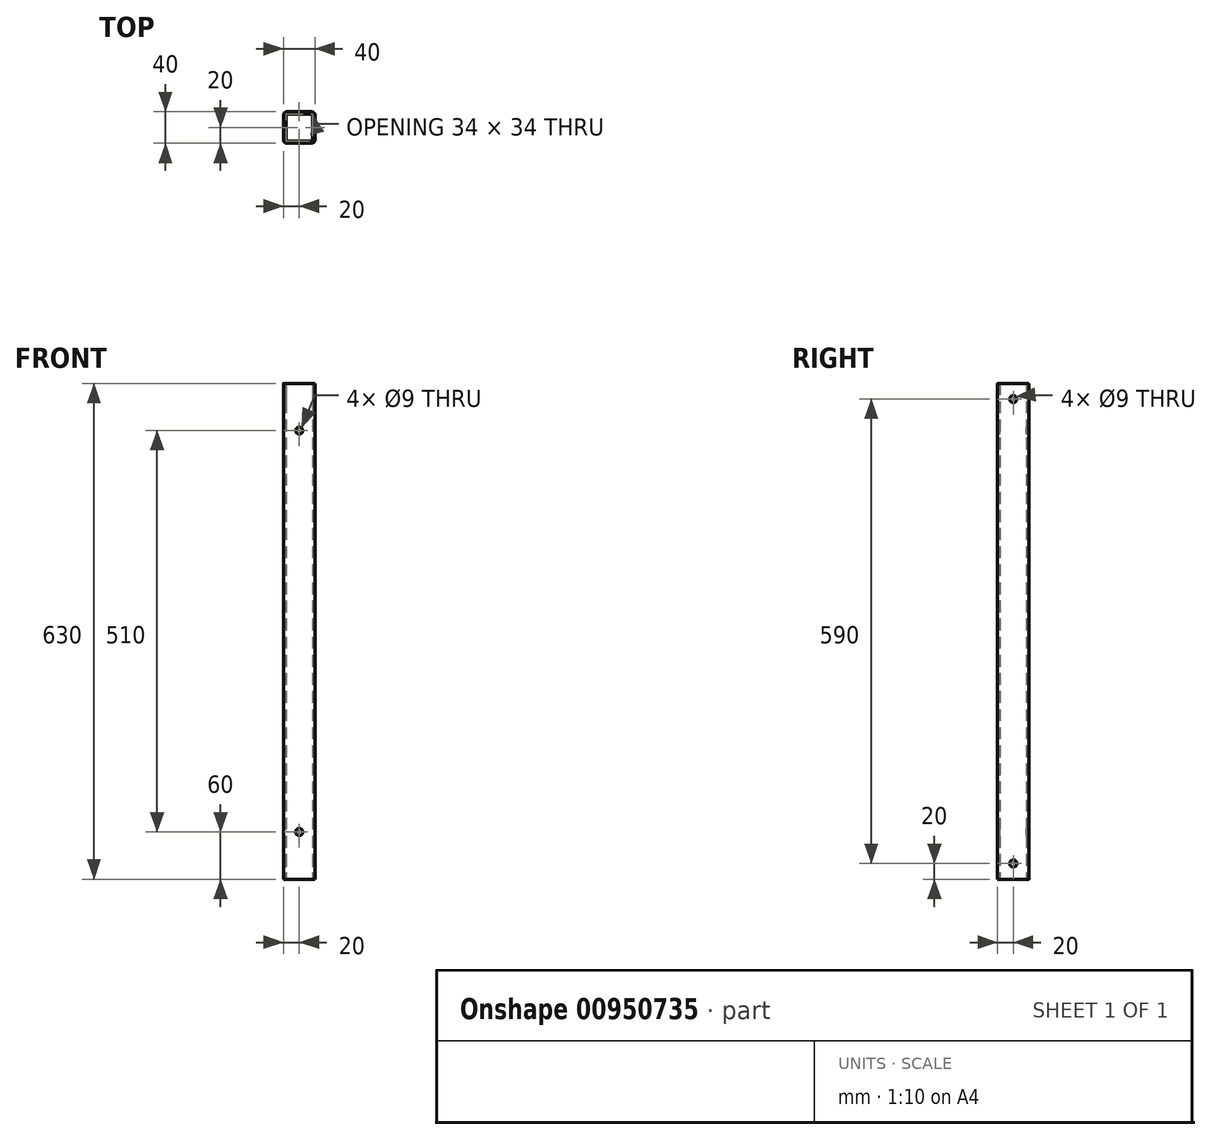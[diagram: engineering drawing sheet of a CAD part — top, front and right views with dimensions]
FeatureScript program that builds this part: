
annotation { "Feature Type Name" : "Feature", "Feature Type Description" : "" }
export const myFeature = defineFeature(function(context is Context, id is Id, definition is map)
    precondition{}
    {
        {
            var Q0;
            Q0=qCreatedBy(makeId("Top.planeOp"),FACE);
            var sketch = newSketch(context, id + "F0", { "sketchPlane" : qUnion([Q0])});
            skLineSegment(sketch, "E0.bottom", {"start": v(15.5, -20) * mm, "end": v(-15.5, -20) * mm});
            skLineSegment(sketch, "E0.top", {"start": v(15.5, 20) * mm, "end": v(-15.5, 20) * mm});
            skLineSegment(sketch, "E0.left", {"start": v(20, -15.5) * mm, "end": v(20, 15.5) * mm});
            skLineSegment(sketch, "E0.right", {"start": v(-20, -15.5) * mm, "end": v(-20, 15.5) * mm});
            skPoint(sketch, "E0.middle", {"position": v(0, 0) * mm});
            skPoint(sketch, "E1.visualSharp", {"position": v(-20, 20) * mm});
            skArc(sketch, "E2.filletArc", {"start": v(-15.5, 20) * mm, "mid": v(-18.68, 18.68) * mm, "end": v(-20, 15.5) * mm});
            skPoint(sketch, "E3.visualSharp", {"position": v(20, 20) * mm});
            skArc(sketch, "E3.filletArc", {"start": v(20, 15.5) * mm, "mid": v(18.68, 18.68) * mm, "end": v(15.5, 20) * mm});
            skPoint(sketch, "E4.visualSharp", {"position": v(20, -20) * mm});
            skArc(sketch, "E4.filletArc", {"start": v(15.5, -20) * mm, "mid": v(18.68, -18.68) * mm, "end": v(20, -15.5) * mm});
            skPoint(sketch, "E5.visualSharp", {"position": v(-20, -20) * mm});
            skArc(sketch, "E5.filletArc", {"start": v(-20, -15.5) * mm, "mid": v(-18.68, -18.68) * mm, "end": v(-15.5, -20) * mm});
            skArc(sketch, "E6.0", {"start": v(17, 15.5) * mm, "mid": v(16.56, 16.56) * mm, "end": v(15.5, 17) * mm});
            skLineSegment(sketch, "E6.1", {"start": v(17, -15.5) * mm, "end": v(17, 15.5) * mm});
            skLineSegment(sketch, "E6.2", {"start": v(15.5, 17) * mm, "end": v(-15.5, 17) * mm});
            skArc(sketch, "E6.3", {"start": v(15.5, -17) * mm, "mid": v(16.56, -16.56) * mm, "end": v(17, -15.5) * mm});
            skArc(sketch, "E6.4", {"start": v(-15.5, 17) * mm, "mid": v(-16.56, 16.56) * mm, "end": v(-17, 15.5) * mm});
            skLineSegment(sketch, "E6.5", {"start": v(-17, -15.5) * mm, "end": v(-17, 15.5) * mm});
            skArc(sketch, "E6.6", {"start": v(-17, -15.5) * mm, "mid": v(-16.56, -16.56) * mm, "end": v(-15.5, -17) * mm});
            skLineSegment(sketch, "E6.7", {"start": v(15.5, -17) * mm, "end": v(-15.5, -17) * mm});
            skSolve(sketch);
        }
        {
            var Q0;
            Q0=qSketchRegion(id+"F0",true);
            extrude(context, id + "F1", {"entities" : qUnion([Q0]), "depth" : 630 * mm, "offsetDistance" : 25 * mm});
        }
        {
            var Q0;
            Q0=makeQuery(id+"F1.opExtrude","SWEPT_FACE",FACE,{"disambiguationData":[OSD([sQuery(id+"F0.wireOp",EDGE,"E0.bottom")])]});
            var sketch = newSketch(context, id + "F2", { "sketchPlane" : qUnion([Q0])});
            skLineSegment(sketch, "E7", {"start": v(0, 630) * mm, "end": v(0, 0) * mm, "construction": true});
            skCircle(sketch, "E8", {"center": v(0, 570) * mm, "radius": 4.5 * mm});
            skCircle(sketch, "E9", {"center": v(0, 60) * mm, "radius": 4.5 * mm});
            skSolve(sketch);
        }
        {
            var Q0;
            Q0=qSketchRegion(id+"F2",true);
            extrude(context, id + "F3", {"entities" : qUnion([Q0]), "operationType" : NewBodyOperationType.REMOVE, "endBound" : BoundingType.THROUGH_ALL, "oppositeDirection" : true, "depth" : 25 * mm, "offsetDistance" : 25 * mm});
        }
        {
            var Q0;
            Q0=makeQuery(id+"F1.opExtrude","SWEPT_FACE",FACE,{"disambiguationData":[OSD([sQuery(id+"F0.wireOp",EDGE,"E0.right")])]});
            var sketch = newSketch(context, id + "F4", { "sketchPlane" : qUnion([Q0])});
            skLineSegment(sketch, "E10", {"start": v(0, 0) * mm, "end": v(0, 630) * mm, "construction": true});
            skCircle(sketch, "E11", {"center": v(0, 610) * mm, "radius": 4.5 * mm});
            skCircle(sketch, "E12", {"center": v(0, 20) * mm, "radius": 4.5 * mm});
            skSolve(sketch);
        }
        {
            var Q0;
            Q0=qSketchRegion(id+"F4",true);
            extrude(context, id + "F5", {"entities" : qUnion([Q0]), "operationType" : NewBodyOperationType.REMOVE, "endBound" : BoundingType.THROUGH_ALL, "oppositeDirection" : true, "depth" : 25 * mm, "offsetDistance" : 25 * mm});
        }
    });
